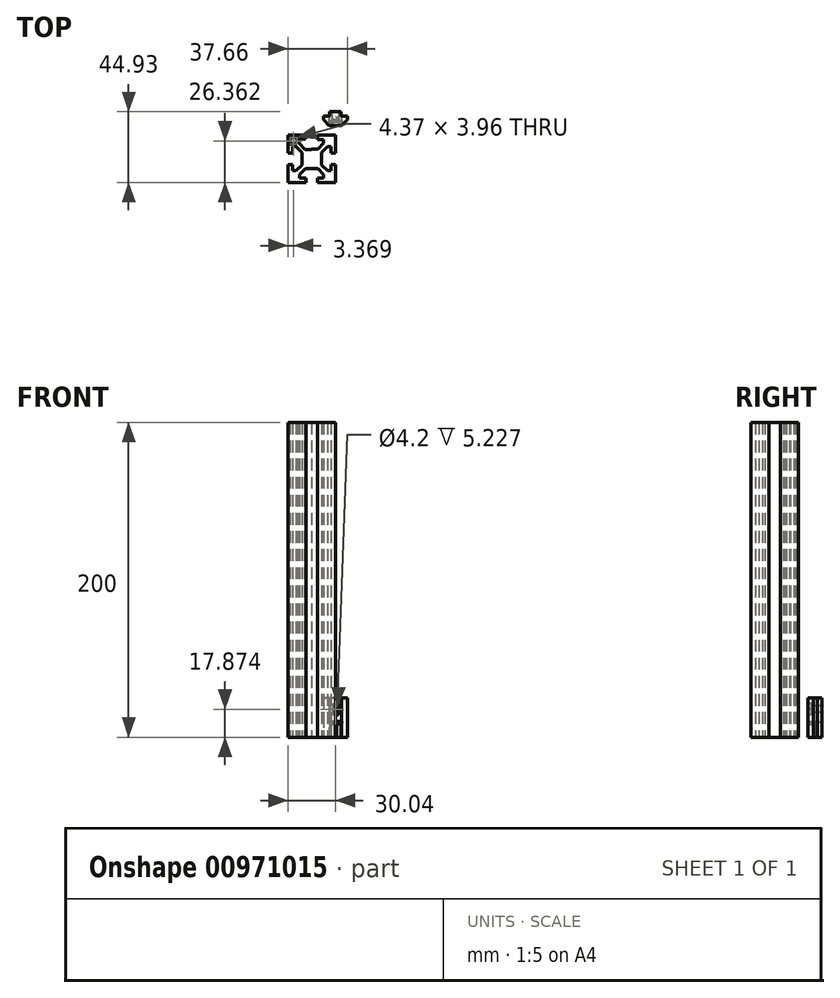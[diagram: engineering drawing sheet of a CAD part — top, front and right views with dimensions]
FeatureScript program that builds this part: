
annotation { "Feature Type Name" : "Feature", "Feature Type Description" : "" }
export const myFeature = defineFeature(function(context is Context, id is Id, definition is map)
    precondition{}
    {
        {
            var Q0;
            Q0=qCreatedBy(makeId("Top.planeOp"),FACE);
            var sketch = newSketch(context, id + "F0", { "sketchPlane" : qUnion([Q0])});
            skLineSegment(sketch, "E0.bottom", {"start": v(15, -15) * mm, "end": v(-15, -15) * mm});
            skLineSegment(sketch, "E0.top", {"start": v(15, 15) * mm, "end": v(-15, 15) * mm});
            skLineSegment(sketch, "E0.left", {"start": v(15, -15) * mm, "end": v(15, 15) * mm});
            skLineSegment(sketch, "E0.right", {"start": v(-15, -15) * mm, "end": v(-15, 15) * mm});
            skPoint(sketch, "E0.middle", {"position": v(0, 0) * mm});
            skLineSegment(sketch, "E1.bottom", {"start": v(-13.81, 13.34) * mm, "end": v(-9.44, 13.34) * mm});
            skLineSegment(sketch, "E1.top", {"start": v(-13.81, 9.38) * mm, "end": v(-9.44, 9.38) * mm});
            skLineSegment(sketch, "E1.left", {"start": v(-13.81, 13.34) * mm, "end": v(-13.81, 9.38) * mm});
            skLineSegment(sketch, "E1.right", {"start": v(-9.44, 13.34) * mm, "end": v(-9.44, 9.38) * mm});
            skLineSegment(sketch, "E2", {"start": v(-4.58, 15) * mm, "end": v(-4.58, 14.31) * mm});
            skLineSegment(sketch, "E3", {"start": v(-4.58, 14.31) * mm, "end": v(-3.96, 14.31) * mm});
            skLineSegment(sketch, "E4", {"start": v(-3.96, 14.31) * mm, "end": v(-3.96, 12.58) * mm});
            skLineSegment(sketch, "E5", {"start": v(-3.96, 12.58) * mm, "end": v(-8.2, 12.58) * mm});
            skLineSegment(sketch, "E6", {"start": v(-8.2, 12.58) * mm, "end": v(-8.2, 9.94) * mm});
            skLineSegment(sketch, "E7", {"start": v(-8.2, 9.94) * mm, "end": v(-4.1, 5.77) * mm});
            skLineSegment(sketch, "E8", {"start": v(-4.1, 5.77) * mm, "end": v(0, 5.77) * mm});
            skLineSegment(sketch, "E9", {"start": v(0, 5.77) * mm, "end": v(0, 15) * mm});
            skLineSegment(sketch, "E10", {"start": v(0, 15) * mm, "end": v(-4.58, 15) * mm});
            skLineSegment(sketch, "E11", {"start": v(-3.61, 15) * mm, "end": v(-3.61, 12.2) * mm});
            skLineSegment(sketch, "E12", {"start": v(-3.61, 12.2) * mm, "end": v(-7.62, 12.2) * mm});
            skLineSegment(sketch, "E13", {"start": v(-7.62, 12.2) * mm, "end": v(-7.62, 9.9) * mm});
            skLineSegment(sketch, "E14", {"start": v(-7.62, 9.9) * mm, "end": v(-3.96, 6.17) * mm});
            skLineSegment(sketch, "E15", {"start": v(-3.96, 6.17) * mm, "end": v(0, 6.17) * mm});
            skLineSegment(sketch, "E16.MirrorCS", {"start": v(3.61, 15) * mm, "end": v(3.61, 12.2) * mm});
            skLineSegment(sketch, "E17.MirrorCS", {"start": v(3.61, 12.2) * mm, "end": v(7.62, 12.2) * mm});
            skLineSegment(sketch, "E18.MirrorCS", {"start": v(7.62, 12.2) * mm, "end": v(7.62, 9.9) * mm});
            skLineSegment(sketch, "E19.MirrorCS", {"start": v(7.62, 9.9) * mm, "end": v(3.96, 6.17) * mm});
            skLineSegment(sketch, "E20.MirrorCS", {"start": v(3.96, 6.17) * mm, "end": v(0, 6.17) * mm});
            skLineSegment(sketch, "E21.MirrorCS", {"start": v(0, 15) * mm, "end": v(4.58, 15) * mm});
            skSolve(sketch);
        }
        {
            var Q0;
            {var subQ0=sQuery(id+"F0.wireOp",EDGE,"E11");Q0=makeQuery(id+"F0.imprint","IMPRINT",FACE,{"disambiguationData":[TD([[makeQuery(id+"F0.imprint","IMPRINT",EDGE,{"derivedFrom":subQ0}),1.0]])]});}
            var Q1;
            {var subQ0=sQuery(id+"F0.wireOp",EDGE,"E16.MirrorCS");Q1=makeQuery(id+"F0.imprint","IMPRINT",FACE,{"disambiguationData":[TD([[makeQuery(id+"F0.imprint","IMPRINT",EDGE,{"derivedFrom":subQ0}),-1.0]])]});}
            extrude(context, id + "F1", {"entities" : qUnion([Q0, Q1]), "depth" : 25 * mm, "offsetDistance" : 25 * mm});
        }
        {
            var Q0;
            Q0=qCreatedBy(makeId("Top.planeOp"),FACE);
            var sketch = newSketch(context, id + "F2", { "sketchPlane" : qUnion([Q0])});
            skCircle(sketch, "E22", {"center": v(0, 8.76) * mm, "radius": 2.7 * mm});
            skCircle(sketch, "E23", {"center": v(0, 8.76) * mm, "radius": 4.45 * mm});
            skSolve(sketch);
        }
        {
            var Q0;
            Q0=makeQuery(id+"F2.imprint","IMPRINT",FACE,{"disambiguationData":[TD([[makeQuery(id+"F2.imprint","IMPRINT",EDGE,{"derivedFrom":sQuery(id+"F2.wireOp",EDGE,"E22")}),1.0]])]});
            extrude(context, id + "F3", {"entities" : qUnion([Q0]), "operationType" : NewBodyOperationType.REMOVE, "depth" : 10 * mm, "offsetDistance" : 25 * mm});
        }
        {
            var Q0;
            Q0=makeQuery(id+"F1.opExtrude","SWEPT_FACE",FACE,{"disambiguationData":[OSD([sQuery(id+"F0.wireOp",EDGE,"E15"),sQuery(id+"F0.wireOp",EDGE,"E20.MirrorCS")])]});
            var sketch = newSketch(context, id + "F4", { "sketchPlane" : qUnion([Q0])});
            skCircle(sketch, "E24", {"center": v(0, 17.87) * mm, "radius": 2.1 * mm});
            skCircle(sketch, "E25.cCircle", {"center": v(0, 17.87) * mm, "radius": 3.5 * mm, "construction": true});
            skLineSegment(sketch, "E25.0", {"start": v(4.04, 17.92) * mm, "end": v(2.06, 14.4) * mm});
            skLineSegment(sketch, "E25.1", {"start": v(2.06, 14.4) * mm, "end": v(-1.98, 14.35) * mm});
            skLineSegment(sketch, "E25.2", {"start": v(-1.98, 14.35) * mm, "end": v(-4.04, 17.83) * mm});
            skLineSegment(sketch, "E25.3", {"start": v(-4.04, 17.83) * mm, "end": v(-2.06, 21.35) * mm});
            skLineSegment(sketch, "E25.4", {"start": v(-2.06, 21.35) * mm, "end": v(1.98, 21.4) * mm});
            skLineSegment(sketch, "E25.5", {"start": v(1.98, 21.4) * mm, "end": v(4.04, 17.92) * mm});
            skPoint(sketch, "E25.0.midPoint", {"position": v(3.05, 16.16) * mm});
            skSolve(sketch);
        }
        {
            var Q0;
            Q0 = qSketchRegion(id + "F4", true);
            extrude(context, id + "F5", {"entities" : qUnion([Q0]), "operationType" : NewBodyOperationType.REMOVE, "oppositeDirection" : true, "depth" : 3.7 * mm, "offsetDistance" : 25 * mm});
        }
        {
            var Q0;
            Q0=makeQuery(id+"F4.imprint","IMPRINT",FACE,{"disambiguationData":[TD([[makeQuery(id+"F4.imprint","IMPRINT",EDGE,{"derivedFrom":sQuery(id+"F4.wireOp",EDGE,"E24")}),1.0]])]});
            extrude(context, id + "F6", {"entities" : qUnion([Q0]), "operationType" : NewBodyOperationType.REMOVE, "oppositeDirection" : true, "depth" : 25 * mm, "offsetDistance" : 25 * mm});
        }
        {
            var Q0;
            Q0=makeQuery(id+"F2.imprint","IMPRINT",FACE,{"disambiguationData":[TD([[makeQuery(id+"F2.imprint","IMPRINT",EDGE,{"derivedFrom":sQuery(id+"F2.wireOp",EDGE,"E22")}),-1.0]])]});
            var Q1;
            Q1=makeQuery(id+"F2.imprint","IMPRINT",FACE,{"disambiguationData":[TD([[makeQuery(id+"F2.imprint","IMPRINT",EDGE,{"derivedFrom":sQuery(id+"F2.wireOp",EDGE,"E22")}),1.0]])]});
            extrude(context, id + "F7", {"entities" : qUnion([Q0, Q1]), "operationType" : NewBodyOperationType.REMOVE, "depth" : 10 * mm, "offsetDistance" : 25 * mm, "hasSecondDirection" : true, "secondDirectionOppositeDirection" : false, "secondDirectionDepth" : 8 * mm});
        }
        {
            var Q0;
            Q0=makeQuery(id+"F7.boolean.opBoolean","COPY",EDGE,{"derivedFrom":makeQuery(id+"F7.opExtrude","CAP_EDGE",EDGE,{"disambiguationData":[OSD([sQuery(id+"F2.wireOp",EDGE,"E23")])],"isStart":true})});
            chamfer(context, id + "F8", {"entities" : qUnion([Q0]), "chamferType" : ChamferType.OFFSET_ANGLE, "width" : 1.9 * mm, "oppositeDirection" : false, "angle" : 30 * degree});
        }
        {
            var Q0;
            Q0=makeQuery(id+"F5.boolean.opBoolean","COPY",EDGE,{"derivedFrom":makeQuery(id+"F5.opExtrude","CAP_EDGE",EDGE,{"disambiguationData":[OSD([sQuery(id+"F4.wireOp",EDGE,"E25.5")])],"isStart":false})});
            var Q1;
            Q1=makeQuery(id+"F5.boolean.opBoolean","COPY",EDGE,{"derivedFrom":makeQuery(id+"F5.opExtrude","CAP_EDGE",EDGE,{"disambiguationData":[OSD([sQuery(id+"F4.wireOp",EDGE,"E25.0")])],"isStart":false})});
            var Q2;
            Q2=makeQuery(id+"F5.boolean.opBoolean","COPY",EDGE,{"derivedFrom":makeQuery(id+"F5.opExtrude","CAP_EDGE",EDGE,{"disambiguationData":[OSD([sQuery(id+"F4.wireOp",EDGE,"E25.1")])],"isStart":false})});
            var Q3;
            Q3=makeQuery(id+"F5.boolean.opBoolean","COPY",EDGE,{"derivedFrom":makeQuery(id+"F5.opExtrude","CAP_EDGE",EDGE,{"disambiguationData":[OSD([sQuery(id+"F4.wireOp",EDGE,"E25.2")])],"isStart":false})});
            var Q4;
            Q4=makeQuery(id+"F5.boolean.opBoolean","COPY",EDGE,{"derivedFrom":makeQuery(id+"F5.opExtrude","CAP_EDGE",EDGE,{"disambiguationData":[OSD([sQuery(id+"F4.wireOp",EDGE,"E25.4")])],"isStart":false})});
            var Q5;
            Q5=makeQuery(id+"F5.boolean.opBoolean","COPY",EDGE,{"derivedFrom":makeQuery(id+"F5.opExtrude","CAP_EDGE",EDGE,{"disambiguationData":[OSD([sQuery(id+"F4.wireOp",EDGE,"E25.3")])],"isStart":false})});
            chamfer(context, id + "F9", {"entities" : qUnion([Q0, Q1, Q2, Q3, Q4, Q5]), "width" : 1.5 * mm, "tangentPropagation" : true});
        }
        {
            var Q0;
            Q0=qCreatedBy(makeId("Top.planeOp"),FACE);
            var sketch = newSketch(context, id + "F10", { "sketchPlane" : qUnion([Q0])});
            skLineSegment(sketch, "E26.bottom", {"start": v(-0.04, -29.93) * mm, "end": v(-30.04, -29.93) * mm});
            skLineSegment(sketch, "E26.top", {"start": v(-0.04, 0.07) * mm, "end": v(-30.04, 0.07) * mm});
            skLineSegment(sketch, "E26.left", {"start": v(-0.04, -29.93) * mm, "end": v(-0.04, 0.07) * mm});
            skLineSegment(sketch, "E26.right", {"start": v(-30.04, -29.93) * mm, "end": v(-30.04, 0.07) * mm});
            skPoint(sketch, "E26.middle", {"position": v(-15.04, -14.93) * mm});
            skLineSegment(sketch, "E27.bottom", {"start": v(-28.86, -1.59) * mm, "end": v(-24.48, -1.59) * mm});
            skLineSegment(sketch, "E27.top", {"start": v(-28.86, -5.55) * mm, "end": v(-24.48, -5.55) * mm});
            skLineSegment(sketch, "E27.left", {"start": v(-28.86, -1.59) * mm, "end": v(-28.86, -5.55) * mm});
            skLineSegment(sketch, "E27.right", {"start": v(-24.48, -1.59) * mm, "end": v(-24.48, -5.55) * mm});
            skLineSegment(sketch, "E28", {"start": v(-19.63, 0.07) * mm, "end": v(-19.63, -0.62) * mm});
            skLineSegment(sketch, "E29", {"start": v(-19.63, -0.62) * mm, "end": v(-19, -0.62) * mm});
            skLineSegment(sketch, "E30", {"start": v(-19, -0.62) * mm, "end": v(-19, -2.35) * mm});
            skLineSegment(sketch, "E31", {"start": v(-19, -2.35) * mm, "end": v(-23.24, -2.35) * mm});
            skLineSegment(sketch, "E32", {"start": v(-23.24, -2.35) * mm, "end": v(-23.24, -5) * mm});
            skLineSegment(sketch, "E33", {"start": v(-23.24, -5) * mm, "end": v(-19.14, -9.15) * mm});
            skLineSegment(sketch, "E34", {"start": v(-19.14, -9.15) * mm, "end": v(-15.04, -9.15) * mm});
            skLineSegment(sketch, "E35", {"start": v(-15.04, -9.15) * mm, "end": v(-15.04, 0.07) * mm});
            skLineSegment(sketch, "E36", {"start": v(-15.04, 0.07) * mm, "end": v(-19.63, 0.07) * mm});
            skLineSegment(sketch, "E37", {"start": v(-18.66, 0.07) * mm, "end": v(-18.66, -2.72) * mm});
            skLineSegment(sketch, "E38", {"start": v(-18.66, -2.72) * mm, "end": v(-22.66, -2.72) * mm});
            skLineSegment(sketch, "E39", {"start": v(-22.66, -2.72) * mm, "end": v(-22.66, -5.03) * mm});
            skLineSegment(sketch, "E40", {"start": v(-22.66, -5.03) * mm, "end": v(-19, -8.75) * mm});
            skLineSegment(sketch, "E41", {"start": v(-19, -8.75) * mm, "end": v(2.82, -8.75) * mm});
            skLineSegment(sketch, "E42.MirrorCS", {"start": v(-11.43, 0.07) * mm, "end": v(-11.43, -2.72) * mm});
            skLineSegment(sketch, "E43.MirrorCS", {"start": v(-11.43, -2.72) * mm, "end": v(-7.43, -2.72) * mm});
            skLineSegment(sketch, "E44.MirrorCS", {"start": v(-7.43, -2.72) * mm, "end": v(-7.43, -5.03) * mm});
            skLineSegment(sketch, "E45.MirrorCS", {"start": v(-7.43, -5.03) * mm, "end": v(-11.09, -8.75) * mm});
            skLineSegment(sketch, "E46.MirrorCS", {"start": v(-11.09, -8.75) * mm, "end": v(-32.9, -8.75) * mm});
            skLineSegment(sketch, "E47.MirrorCS", {"start": v(-15.04, 0.07) * mm, "end": v(-10.46, 0.07) * mm});
            skLineSegment(sketch, "E48.1.0", {"start": v(-30.04, -18.54) * mm, "end": v(-27.25, -18.54) * mm});
            skLineSegment(sketch, "E48.1.1", {"start": v(-27.25, -18.54) * mm, "end": v(-27.25, -22.55) * mm});
            skLineSegment(sketch, "E48.1.2", {"start": v(-27.25, -22.55) * mm, "end": v(-24.94, -22.55) * mm});
            skLineSegment(sketch, "E48.1.3", {"start": v(-24.94, -22.55) * mm, "end": v(-21.22, -18.89) * mm});
            skLineSegment(sketch, "E48.1.4", {"start": v(-24.94, -7.31) * mm, "end": v(-21.22, -10.97) * mm});
            skLineSegment(sketch, "E48.1.5", {"start": v(-27.25, -7.31) * mm, "end": v(-24.94, -7.31) * mm});
            skLineSegment(sketch, "E48.1.6", {"start": v(-27.25, -11.31) * mm, "end": v(-27.25, -7.31) * mm});
            skLineSegment(sketch, "E48.1.7", {"start": v(-30.04, -11.31) * mm, "end": v(-27.25, -11.31) * mm});
            skLineSegment(sketch, "E48.1.8", {"start": v(-30.04, -14.93) * mm, "end": v(-30.04, -19.51) * mm});
            skLineSegment(sketch, "E48.1.9", {"start": v(-30.04, -14.93) * mm, "end": v(-30.04, -10.35) * mm});
            skLineSegment(sketch, "E48.1.10", {"start": v(-21.22, -10.97) * mm, "end": v(-21.22, -32.8) * mm});
            skLineSegment(sketch, "E48.2.0", {"start": v(-11.43, -29.93) * mm, "end": v(-11.43, -27.13) * mm});
            skLineSegment(sketch, "E48.2.1", {"start": v(-11.43, -27.13) * mm, "end": v(-7.43, -27.13) * mm});
            skLineSegment(sketch, "E48.2.2", {"start": v(-7.43, -27.13) * mm, "end": v(-7.43, -24.82) * mm});
            skLineSegment(sketch, "E48.2.3", {"start": v(-7.43, -24.82) * mm, "end": v(-11.09, -21.1) * mm});
            skLineSegment(sketch, "E48.2.4", {"start": v(-22.66, -24.82) * mm, "end": v(-19, -21.1) * mm});
            skLineSegment(sketch, "E48.2.5", {"start": v(-22.66, -27.13) * mm, "end": v(-22.66, -24.82) * mm});
            skLineSegment(sketch, "E48.2.6", {"start": v(-18.66, -27.13) * mm, "end": v(-22.66, -27.13) * mm});
            skLineSegment(sketch, "E48.2.7", {"start": v(-18.66, -29.93) * mm, "end": v(-18.66, -27.13) * mm});
            skLineSegment(sketch, "E48.2.8", {"start": v(-15.04, -29.93) * mm, "end": v(-10.46, -29.93) * mm});
            skLineSegment(sketch, "E48.2.9", {"start": v(-15.04, -29.93) * mm, "end": v(-19.63, -29.93) * mm});
            skLineSegment(sketch, "E48.2.10", {"start": v(-19, -21.1) * mm, "end": v(2.82, -21.1) * mm});
            skLineSegment(sketch, "E48.3.0", {"start": v(-0.04, -11.31) * mm, "end": v(-2.84, -11.31) * mm});
            skLineSegment(sketch, "E48.3.1", {"start": v(-2.84, -11.31) * mm, "end": v(-2.84, -7.31) * mm});
            skLineSegment(sketch, "E48.3.2", {"start": v(-2.84, -7.31) * mm, "end": v(-5.15, -7.31) * mm});
            skLineSegment(sketch, "E48.3.3", {"start": v(-5.15, -7.31) * mm, "end": v(-8.87, -10.97) * mm});
            skLineSegment(sketch, "E48.3.4", {"start": v(-5.15, -22.55) * mm, "end": v(-8.87, -18.89) * mm});
            skLineSegment(sketch, "E48.3.5", {"start": v(-2.84, -22.55) * mm, "end": v(-5.15, -22.55) * mm});
            skLineSegment(sketch, "E48.3.6", {"start": v(-2.84, -18.54) * mm, "end": v(-2.84, -22.55) * mm});
            skLineSegment(sketch, "E48.3.7", {"start": v(-0.04, -18.54) * mm, "end": v(-2.84, -18.54) * mm});
            skLineSegment(sketch, "E48.3.8", {"start": v(-0.04, -14.93) * mm, "end": v(-0.04, -10.35) * mm});
            skLineSegment(sketch, "E48.3.9", {"start": v(-0.04, -14.93) * mm, "end": v(-0.04, -19.51) * mm});
            skLineSegment(sketch, "E48.3.10", {"start": v(-8.87, -18.89) * mm, "end": v(-8.87, 2.94) * mm});
            skSolve(sketch);
        }
        {
            var Q0;
            Q0=makeQuery(id+"F10.imprint","IMPRINT",FACE,{"disambiguationData":[TD([[makeQuery(id+"F10.imprint","IMPRINT",EDGE,{"derivedFrom":sQuery(id+"F10.wireOp",EDGE,"E27.bottom")}),1.0]])]});
            var Q1;
            {var subQ16=sQuery(id+"F10.wireOp",EDGE,"E34");Q1=makeQuery(id+"F10.imprint","IMPRINT",FACE,{"disambiguationData":[TD([[makeQuery(id+"F10.imprint","IMPRINT",EDGE,{"derivedFrom":subQ16}),-1.0]])]});}
            var Q2;
            {var subQ0=sQuery(id+"F10.wireOp",EDGE,"E48.1.7");Q2=makeQuery(id+"F10.imprint","IMPRINT",FACE,{"disambiguationData":[TD([[makeQuery(id+"F10.imprint","IMPRINT",EDGE,{"derivedFrom":subQ0}),1.0]])]});}
            var Q3;
            {var subQ2=sQuery(id+"F10.wireOp",EDGE,"E44.MirrorCS");Q3=makeQuery(id+"F10.imprint","IMPRINT",FACE,{"disambiguationData":[TD([[makeQuery(id+"F10.imprint","IMPRINT",EDGE,{"derivedFrom":subQ2}),1.0]])]});}
            var Q4;
            {var subQ0=sQuery(id+"F10.wireOp",EDGE,"E48.3.0");Q4=makeQuery(id+"F10.imprint","IMPRINT",FACE,{"disambiguationData":[TD([[makeQuery(id+"F10.imprint","IMPRINT",EDGE,{"derivedFrom":subQ0}),-1.0]])]});}
            var Q5;
            {var subQ0=sQuery(id+"F10.wireOp",EDGE,"E48.3.7");Q5=makeQuery(id+"F10.imprint","IMPRINT",FACE,{"disambiguationData":[TD([[makeQuery(id+"F10.imprint","IMPRINT",EDGE,{"derivedFrom":subQ0}),1.0]])]});}
            var Q6;
            {var subQ13=sQuery(id+"F10.wireOp",EDGE,"E48.2.0");Q6=makeQuery(id+"F10.imprint","IMPRINT",FACE,{"disambiguationData":[TD([[makeQuery(id+"F10.imprint","IMPRINT",EDGE,{"derivedFrom":subQ13}),-1.0]])]});}
            var Q7;
            {var subQ13=sQuery(id+"F10.wireOp",EDGE,"E48.1.0");Q7=makeQuery(id+"F10.imprint","IMPRINT",FACE,{"disambiguationData":[TD([[makeQuery(id+"F10.imprint","IMPRINT",EDGE,{"derivedFrom":subQ13}),-1.0]])]});}
            var Q8;
            {var subQ0=sQuery(id+"F10.wireOp",EDGE,"E48.2.7");Q8=makeQuery(id+"F10.imprint","IMPRINT",FACE,{"disambiguationData":[TD([[makeQuery(id+"F10.imprint","IMPRINT",EDGE,{"derivedFrom":subQ0}),1.0]])]});}
            var Q9;
            {var subQ1=sQuery(id+"F10.wireOp",EDGE,"E42.MirrorCS");Q9=makeQuery(id+"F10.imprint","IMPRINT",FACE,{"disambiguationData":[TD([[makeQuery(id+"F10.imprint","IMPRINT",EDGE,{"derivedFrom":subQ1}),1.0]])]});}
            var Q10;
            {var subQ1=sQuery(id+"F10.wireOp",EDGE,"E41");var subQ3=sQuery(id+"F10.wireOp",EDGE,"E48.3.10");var subQ4=makeQuery(id+"F10.imprint","INTERSECT",VERTEX,{"derivedFrom":[subQ1,subQ3]});Q10=makeQuery(id+"F10.imprint","IMPRINT",FACE,{"disambiguationData":[TD([[makeQuery(id+"F10.imprint","IMPRINT",EDGE,{"disambiguationData":[TD([[subQ4,-1.0]])],"derivedFrom":subQ3}),1.0]])]});}
            var Q11;
            {var subQ0=sQuery(id+"F10.wireOp",EDGE,"E48.3.10");var subQ1=sQuery(id+"F10.wireOp",EDGE,"E41");var subQ2=makeQuery(id+"F10.imprint","INTERSECT",VERTEX,{"derivedFrom":[subQ1,subQ0]});Q11=makeQuery(id+"F10.imprint","IMPRINT",FACE,{"disambiguationData":[TD([[makeQuery(id+"F10.imprint","IMPRINT",EDGE,{"disambiguationData":[TD([[subQ2,-1.0]])],"derivedFrom":subQ1}),-1.0]])]});}
            extrude(context, id + "F11", {"entities" : qUnion([Q0, Q1, Q2, Q3, Q4, Q5, Q6, Q7, Q8, Q9, Q10, Q11]), "depth" : 200 * mm, "offsetDistance" : 25 * mm});
        }
    });
